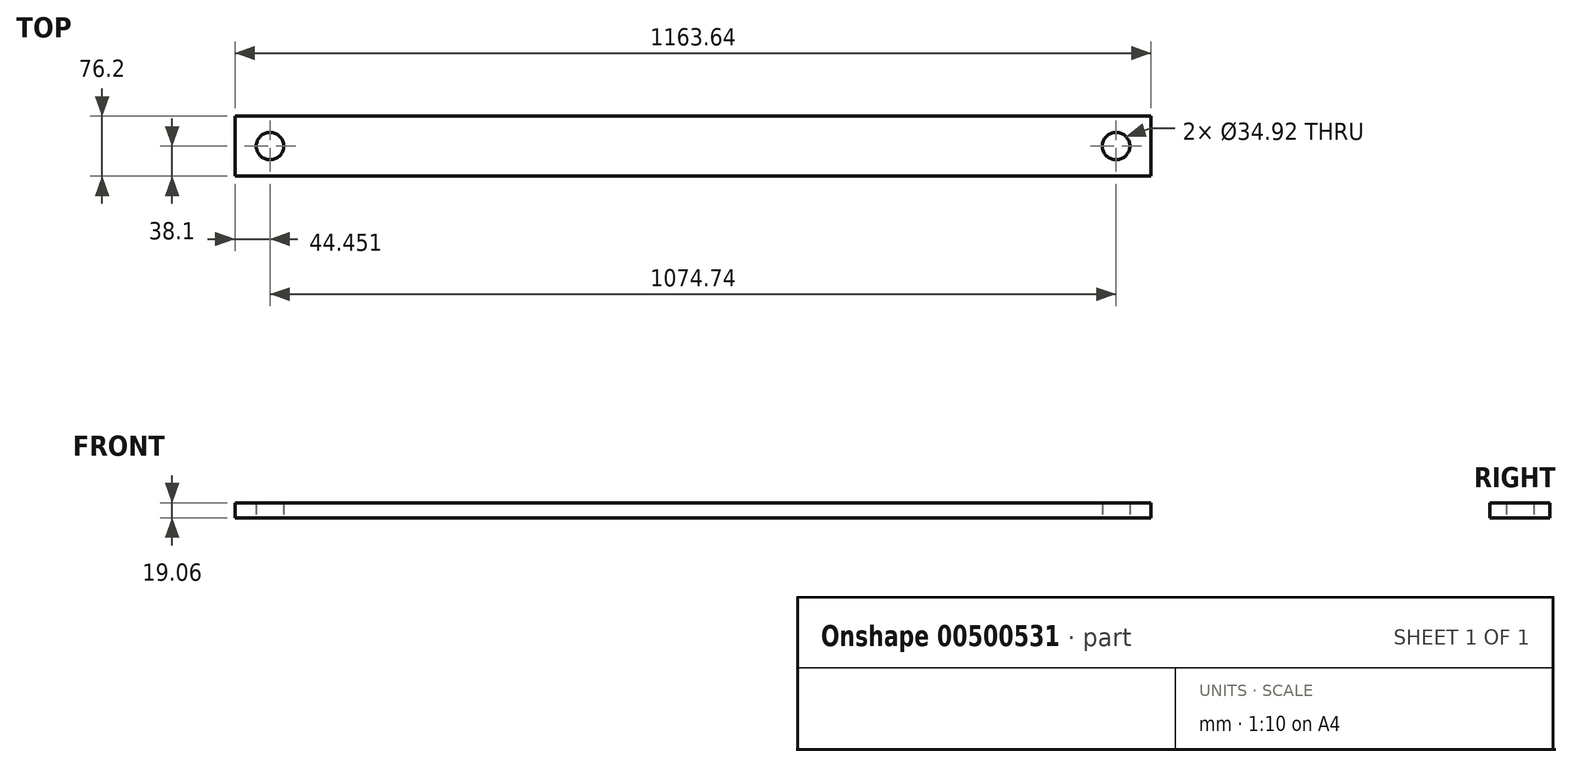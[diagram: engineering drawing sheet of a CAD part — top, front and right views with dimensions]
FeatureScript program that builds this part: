
annotation { "Feature Type Name" : "Feature", "Feature Type Description" : "" }
export const myFeature = defineFeature(function(context is Context, id is Id, definition is map)
    precondition{}
    {
        {
            var Q0;
            Q0=qCreatedBy(makeId("Top.planeOp"),FACE);
            var sketch = newSketch(context, id + "F0", { "sketchPlane" : qUnion([Q0])});
            skLineSegment(sketch, "E0.bottom", {"start": v(581.82, -38.1) * mm, "end": v(-581.82, -38.1) * mm});
            skLineSegment(sketch, "E0.top", {"start": v(581.82, 38.1) * mm, "end": v(-581.82, 38.1) * mm});
            skLineSegment(sketch, "E0.left", {"start": v(581.82, -38.1) * mm, "end": v(581.82, 38.1) * mm});
            skLineSegment(sketch, "E0.right", {"start": v(-581.82, -38.1) * mm, "end": v(-581.82, 38.1) * mm});
            skPoint(sketch, "E0.middle", {"position": v(0, 0) * mm});
            skCircle(sketch, "E1", {"center": v(-537.37, 0) * mm, "radius": 17.46 * mm});
            skCircle(sketch, "E2.MirrorC", {"center": v(537.37, 0) * mm, "radius": 17.46 * mm});
            skSolve(sketch);
        }
        {
            var Q0;
            Q0 = qSketchRegion(id + "F0", true);
            extrude(context, id + "F1", {"entities" : qUnion([Q0]), "endBound" : BoundingType.SYMMETRIC, "depth" : 19.05 * mm});
        }
    });
